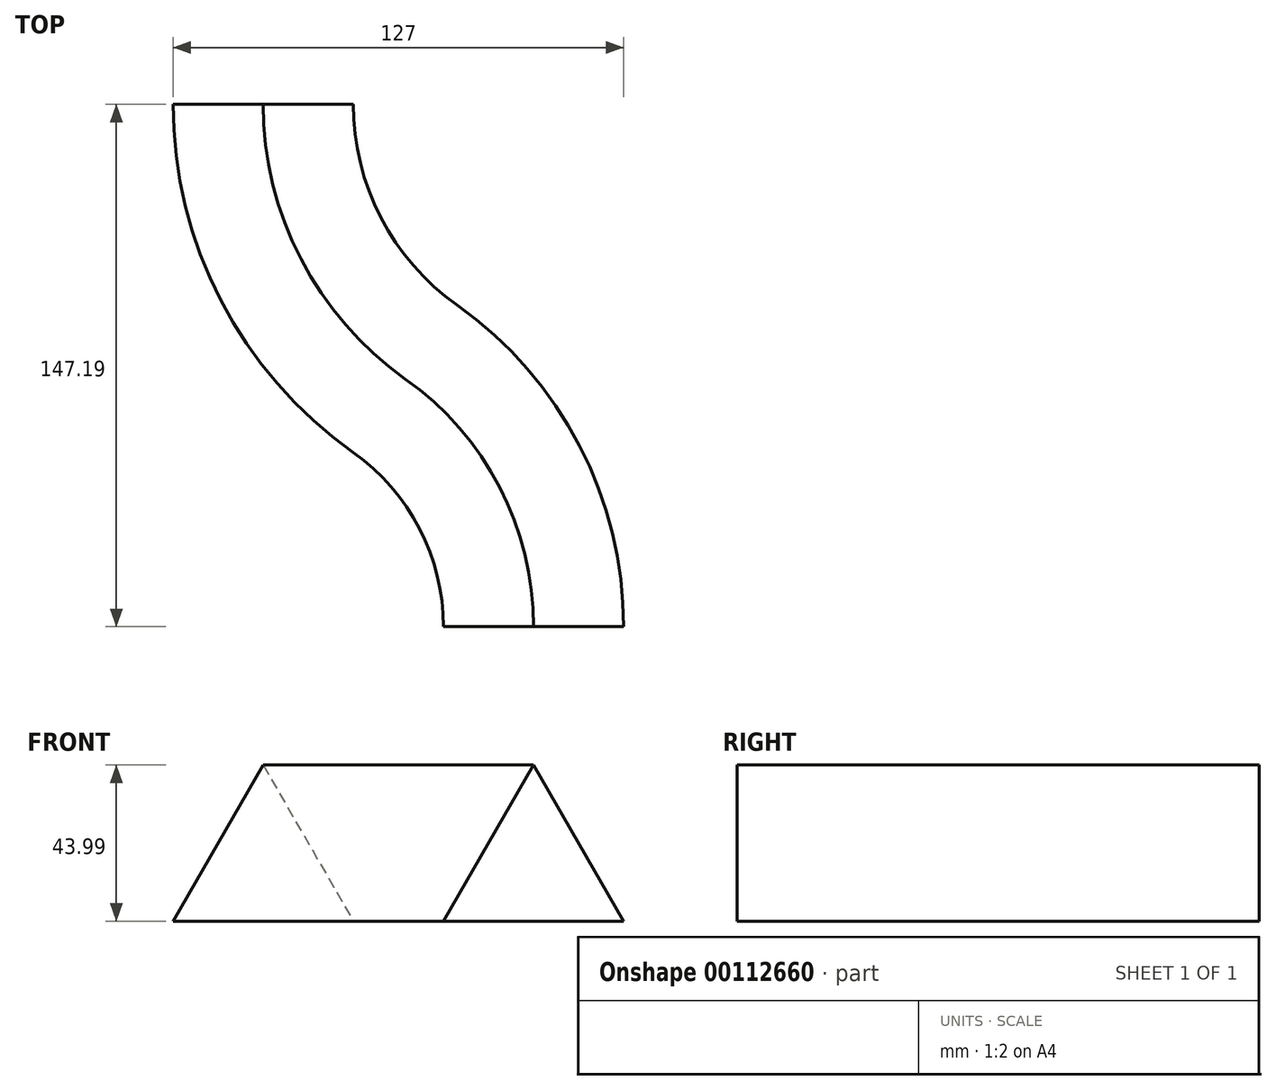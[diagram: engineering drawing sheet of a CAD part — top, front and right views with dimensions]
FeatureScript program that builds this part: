
annotation { "Feature Type Name" : "Feature", "Feature Type Description" : "" }
export const myFeature = defineFeature(function(context is Context, id is Id, definition is map)
    precondition{}
    {
        {
            var Q0;
            Q0=qCreatedBy(makeId("Top.planeOp"),FACE);
            var sketch = newSketch(context, id + "F0", { "sketchPlane" : qUnion([Q0])});
            skLineSegment(sketch, "E0", {"start": v(0, 0) * mm, "end": v(-25.4, 0) * mm, "construction": true});
            skLineSegment(sketch, "E1", {"start": v(-25.4, 0) * mm, "end": v(-25.4, 49.06) * mm, "construction": true});
            skLineSegment(sketch, "E2", {"start": v(-25.4, 49.06) * mm, "end": v(-76.2, 49.06) * mm, "construction": true});
            skArc(sketch, "E3", {"start": v(0, 0) * mm, "mid": v(-6.73, 27.62) * mm, "end": v(-25.4, 49.06) * mm});
            skLineSegment(sketch, "E4", {"start": v(-76.2, 49.06) * mm, "end": v(-76.2, 147.2) * mm});
            skArc(sketch, "E5", {"start": v(-76.2, 147.2) * mm, "mid": v(-62.75, 91.94) * mm, "end": v(-25.4, 49.06) * mm});
            skLineSegment(sketch, "E6", {"start": v(0, 0) * mm, "end": v(0, -25.4) * mm, "construction": true});
            skLineSegment(sketch, "E7", {"start": v(101.6, 147.2) * mm, "end": v(101.6, 0) * mm, "construction": true});
            skLineSegment(sketch, "E8", {"start": v(-76.2, 147.2) * mm, "end": v(-25.4, 147.2) * mm, "construction": true});
            skLineSegment(sketch, "E9", {"start": v(-25.4, 147.2) * mm, "end": v(101.6, 147.2) * mm, "construction": true});
            skLineSegment(sketch, "E10", {"start": v(0, 0) * mm, "end": v(50.8, 0) * mm, "construction": true});
            skLineSegment(sketch, "E11", {"start": v(50.8, 0) * mm, "end": v(101.6, 0) * mm, "construction": true});
            skArc(sketch, "E12", {"start": v(50.8, 0) * mm, "mid": v(38.39, 50.98) * mm, "end": v(3.93, 90.54) * mm});
            skArc(sketch, "E13", {"start": v(-25.4, 147.2) * mm, "mid": v(-17.63, 115.3) * mm, "end": v(3.93, 90.54) * mm});
            skSolve(sketch);
        }
        {
            var Q0;
            Q0=qCreatedBy(makeId("Front.planeOp"),FACE);
            var sketch = newSketch(context, id + "F1", { "sketchPlane" : qUnion([Q0])});
            skCircle(sketch, "E14.cCircle", {"center": v(25.4, 14.66) * mm, "radius": 14.66 * mm, "construction": true});
            skLineSegment(sketch, "E14.0", {"start": v(50.8, 0) * mm, "end": v(0, 0) * mm});
            skLineSegment(sketch, "E14.1", {"start": v(0, 0) * mm, "end": v(25.4, 44) * mm});
            skLineSegment(sketch, "E14.2", {"start": v(25.4, 44) * mm, "end": v(50.8, 0) * mm});
            skPoint(sketch, "E14.0.midPoint", {"position": v(25.4, 0) * mm});
            skSolve(sketch);
        }
        {
            var Q0;
            Q0=makeQuery(id+"F1.imprint","IMPRINT",FACE,{"disambiguationData":[TD([[makeQuery(id+"F1.imprint","IMPRINT",EDGE,{"derivedFrom":sQuery(id+"F1.wireOp",EDGE,"E14.0")}),-1.0]])]});
            var Q1;
            Q1=sQuery(id+"F0.wireOp",EDGE,"E3");
            var Q2;
            Q2=sQuery(id+"F0.wireOp",EDGE,"E5");
            sweep(context, id + "F2", {"profiles" : qUnion([Q0]), "path" : qUnion([Q1, Q2])});
        }
    });
